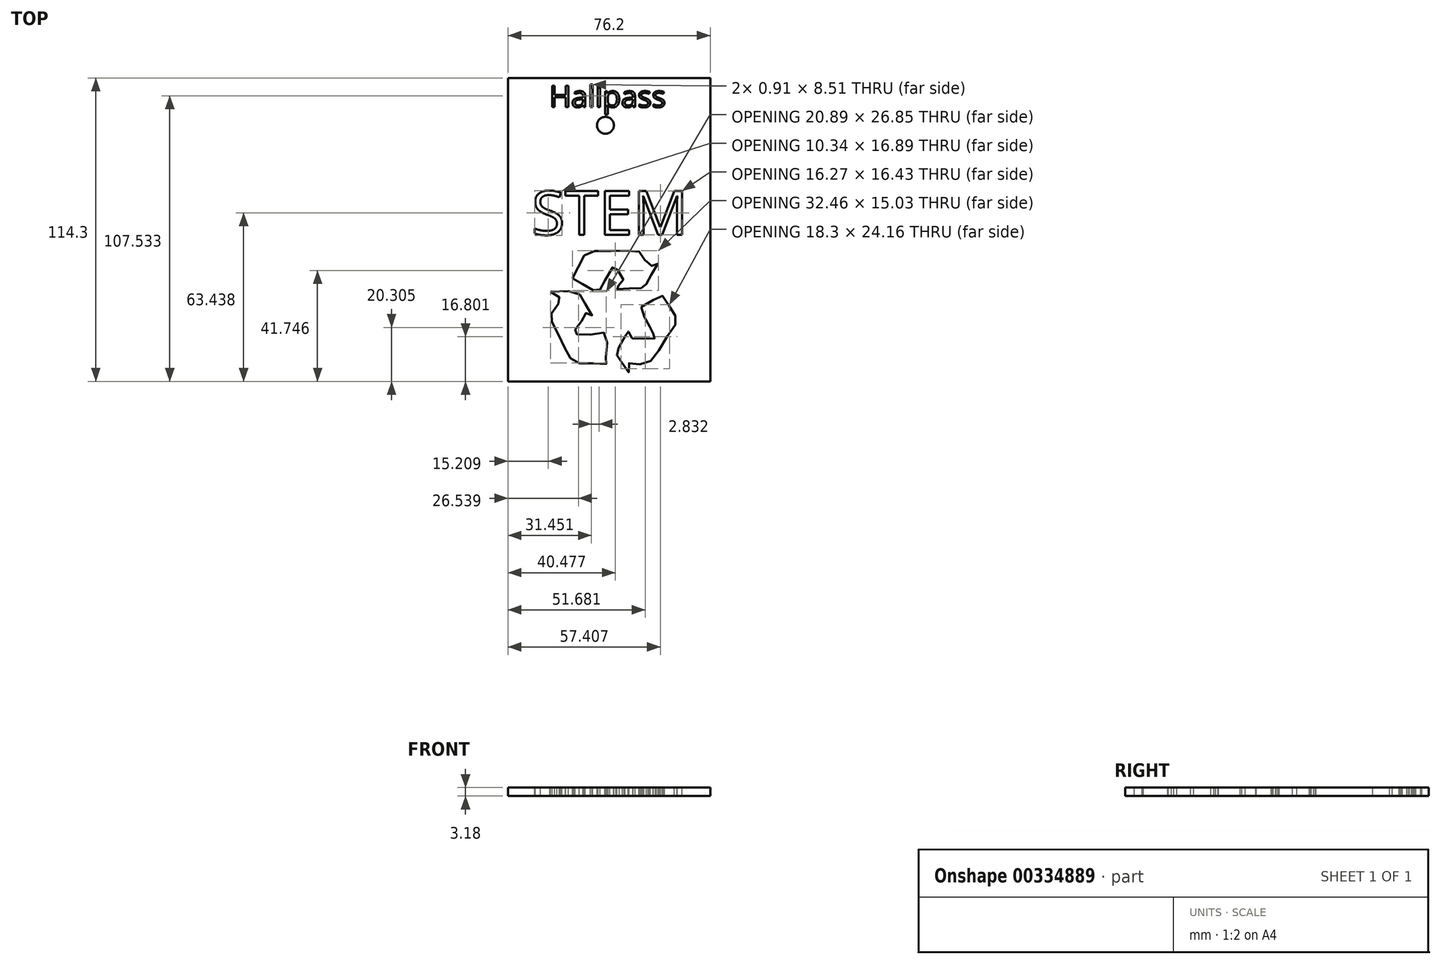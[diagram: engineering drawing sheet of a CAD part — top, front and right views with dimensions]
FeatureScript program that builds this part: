
annotation { "Feature Type Name" : "Feature", "Feature Type Description" : "" }
export const myFeature = defineFeature(function(context is Context, id is Id, definition is map)
    precondition{}
    {
        {
            var Q0;
            Q0=qCreatedBy(makeId("Top.planeOp"),FACE);
            var sketch = newSketch(context, id + "F0", { "sketchPlane" : qUnion([Q0])});
            skLineSegment(sketch, "E0.bottom", {"start": v(-36.95, 59.08) * mm, "end": v(39.25, 59.08) * mm});
            skLineSegment(sketch, "E0.top", {"start": v(-36.95, -55.22) * mm, "end": v(39.25, -55.22) * mm});
            skLineSegment(sketch, "E0.left", {"start": v(-36.95, 59.08) * mm, "end": v(-36.95, -55.22) * mm});
            skLineSegment(sketch, "E0.right", {"start": v(39.25, 59.08) * mm, "end": v(39.25, -55.22) * mm});
            skSolve(sketch);
        }
        {
            var Q0;
            Q0 = qSketchRegion(id + "F0", true);
            extrude(context, id + "F1", {"entities" : qUnion([Q0]), "depth" : 3.17 * mm});
        }
        {
            var Q0;
            Q0=makeQuery(id+"F1.opExtrude","CAP_FACE",FACE,{"disambiguationData":[OSD([sQuery(id+"F0.wireOp",EDGE,"E0.bottom"),sQuery(id+"F0.wireOp",EDGE,"E0.top"),sQuery(id+"F0.wireOp",EDGE,"E0.left"),sQuery(id+"F0.wireOp",EDGE,"E0.right")])],"isStart":false});
            var sketch = newSketch(context, id + "F2", { "sketchPlane" : qUnion([Q0])});
            skCircle(sketch, "E1", {"center": v(-0.25, 41.23) * mm, "radius": 3.18 * mm});
            skSolve(sketch);
        }
        {
            var Q0;
            Q0 = qSketchRegion(id + "F2", true);
            extrude(context, id + "F3", {"entities" : qUnion([Q0]), "operationType" : NewBodyOperationType.REMOVE, "oppositeDirection" : true, "depth" : 3.17 * mm});
        }
        {
            var Q0;
            Q0=makeQuery(id+"F1.opExtrude","CAP_FACE",FACE,{"disambiguationData":[OSD([sQuery(id+"F0.wireOp",EDGE,"E0.bottom"),sQuery(id+"F0.wireOp",EDGE,"E0.top"),sQuery(id+"F0.wireOp",EDGE,"E0.left"),sQuery(id+"F0.wireOp",EDGE,"E0.right")])],"isStart":false});
            var sketch = newSketch(context, id + "F4", { "sketchPlane" : qUnion([Q0])});
            skText(sketch, "E2", { "text": "STEM\n", "fontName": "OpenSans-Regular.ttf"});
            const initialGuessF4  = {"E2": [-0.0281, 0, 1, 0, 0.01657]};
            skSetInitialGuess(sketch, initialGuessF4);
            skSolve(sketch);
        }
        {
            var Q0;
            Q0 = qSketchRegion(id + "F4", true);
            extrude(context, id + "F5", {"entities" : qUnion([Q0]), "operationType" : NewBodyOperationType.REMOVE, "oppositeDirection" : true, "depth" : 3.17 * mm});
        }
        {
            var Q0;
            Q0=qCreatedBy(makeId("Top.planeOp"),FACE);
            var sketch = newSketch(context, id + "F6", { "sketchPlane" : qUnion([Q0])});
            skFitSpline(sketch, "E3", {"points": [v(-12.7, -16.35) * mm, v(-10.74, -17.59) * mm, v(-8.92, -18.6) * mm, v(-7.1, -19.55) * mm, v(-4.78, -20.86) * mm, v(-2.9, -21.88) * mm, v(-2.6, -21.3) * mm, v(-1.8, -19.77) * mm, v(-1.07, -18.46) * mm, v(0, -16.43) * mm, v(1.76, -13.74) * mm, v(3, -11.41) * mm, v(3.58, -11.92) * mm, v(4.38, -13.3) * mm, v(5.25, -14.68) * mm, v(6.27, -16.64) * mm, v(7, -17.73) * mm, v(5.9, -18.53) * mm, v(3.65, -19.84) * mm, v(2.7, -20.35) * mm, v(4.3, -20.42) * mm, v(6.56, -20.35) * mm, v(8.66, -20.2) * mm, v(10.92, -20.13) * mm, v(13.39, -20.13) * mm, v(14.48, -20.06) * mm, v(14.62, -19.62) * mm, v(15.13, -18.68) * mm, v(15.79, -17.3) * mm, v(16.73, -15.55) * mm, v(17.67, -13.67) * mm, v(19.2, -11.41) * mm, v(19.85, -10.1) * mm, v(18.98, -10.54) * mm, v(16.3, -12) * mm, v(15.35, -10.69) * mm, v(14.33, -9.16) * mm, v(13.24, -7.7) * mm, v(12.66, -6.47) * mm, v(11.06, -5.89) * mm, v(8.74, -5.96) * mm, v(4.74, -6.03) * mm, v(0, -6.1) * mm, v(-3.98, -6.03) * mm, v(-6.96, -6.76) * mm, v(-7.98, -7.56) * mm, v(-9, -9.45) * mm, v(-10.45, -12.21) * mm, v(-12.2, -15.2) * mm, v(-12.7, -16.35) * mm]});
            skSolve(sketch);
        }
        {
            var Q0;
            Q0 = qSketchRegion(id + "F6", true);
            extrude(context, id + "F7", {"entities" : qUnion([Q0]), "operationType" : NewBodyOperationType.REMOVE, "depth" : 3.17 * mm});
        }
        {
            var Q0;
            Q0=makeQuery(id+"F1.opExtrude","CAP_FACE",FACE,{"disambiguationData":[OSD([sQuery(id+"F0.wireOp",EDGE,"E0.bottom"),sQuery(id+"F0.wireOp",EDGE,"E0.top"),sQuery(id+"F0.wireOp",EDGE,"E0.left"),sQuery(id+"F0.wireOp",EDGE,"E0.right")])],"isStart":false});
            var sketch = newSketch(context, id + "F8", { "sketchPlane" : qUnion([Q0])});
            skFitSpline(sketch, "E4", {"points": [v(13.23, -27.15) * mm, v(18.2, -24.29) * mm, v(20.94, -22.92) * mm, v(23.32, -25.93) * mm, v(25.33, -29.32) * mm, v(26.7, -32.32) * mm, v(25.33, -34.96) * mm, v(21.32, -40.98) * mm, v(17.8, -46.62) * mm, v(14.8, -48.5) * mm, v(10.53, -48.62) * mm, v(8.4, -48.62) * mm, v(8.53, -51.76) * mm, v(6.65, -49.38) * mm, v(5.14, -46.62) * mm, v(3.76, -44.74) * mm, v(4.52, -42.98) * mm, v(6.65, -39.22) * mm, v(8.4, -35.7) * mm, v(8.4, -38.47) * mm, v(10.4, -38.97) * mm, v(14.17, -39.1) * mm, v(17.93, -39.1) * mm, v(18.93, -38.72) * mm, v(17.93, -37.59) * mm, v(16.93, -35.83) * mm, v(16.05, -33.58) * mm, v(13.8, -30.07) * mm, v(13.23, -27.15) * mm]});
            skSolve(sketch);
        }
        {
            var Q0;
            Q0 = qSketchRegion(id + "F8", true);
            extrude(context, id + "F9", {"entities" : qUnion([Q0]), "operationType" : NewBodyOperationType.REMOVE, "oppositeDirection" : true, "depth" : 3.17 * mm});
        }
        {
            var Q0;
            Q0=makeQuery(id+"F1.opExtrude","CAP_FACE",FACE,{"disambiguationData":[OSD([sQuery(id+"F0.wireOp",EDGE,"E0.bottom"),sQuery(id+"F0.wireOp",EDGE,"E0.top"),sQuery(id+"F0.wireOp",EDGE,"E0.left"),sQuery(id+"F0.wireOp",EDGE,"E0.right")])],"isStart":false});
            var sketch = newSketch(context, id + "F10", { "sketchPlane" : qUnion([Q0])});
            skFitSpline(sketch, "E5", {"points": [v(-20.86, -21.5) * mm, v(-10.36, -21.84) * mm, v(-9.9, -22.53) * mm, v(-7.37, -26.68) * mm, v(-5.3, -30.48) * mm, v(-7.25, -29.45) * mm, v(-8.87, -31.64) * mm, v(-10.02, -33.71) * mm, v(-12.2, -37.06) * mm, v(-11.06, -37.52) * mm, v(-4.6, -37.52) * mm, v(0, -37.29) * mm, v(0, -43.97) * mm, v(0, -47.78) * mm, v(0, -48.7) * mm, v(-5.3, -48.36) * mm, v(-11.4, -48.12) * mm, v(-14.05, -45.47) * mm, v(-16.6, -40.52) * mm, v(-20.05, -33.48) * mm, v(-21.09, -30.71) * mm, v(-18.78, -27.26) * mm, v(-17.4, -24.49) * mm, v(-17.86, -23.34) * mm, v(-20.86, -21.5) * mm]});
            skSolve(sketch);
        }
        {
            var Q0;
            Q0 = qSketchRegion(id + "F10", true);
            extrude(context, id + "F11", {"entities" : qUnion([Q0]), "operationType" : NewBodyOperationType.REMOVE, "oppositeDirection" : true, "depth" : 3.17 * mm});
        }
        {
            var Q0;
            Q0=makeQuery(id+"F1.opExtrude","CAP_FACE",FACE,{"disambiguationData":[OSD([sQuery(id+"F0.wireOp",EDGE,"E0.bottom"),sQuery(id+"F0.wireOp",EDGE,"E0.top"),sQuery(id+"F0.wireOp",EDGE,"E0.left"),sQuery(id+"F0.wireOp",EDGE,"E0.right")])],"isStart":false});
            var sketch = newSketch(context, id + "F12", { "sketchPlane" : qUnion([Q0])});
            skText(sketch, "E6", { "text": "Hallpass\n", "fontName": "OpenSans-Regular.ttf"});
            const initialGuessF12  = {"E6": [-0.0214, 0.04806, 1, 0, 0.00806]};
            skSetInitialGuess(sketch, initialGuessF12);
            skSolve(sketch);
        }
        {
            var Q0;
            Q0 = qSketchRegion(id + "F12", true);
            extrude(context, id + "F13", {"entities" : qUnion([Q0]), "operationType" : NewBodyOperationType.REMOVE, "oppositeDirection" : true, "depth" : 3.17 * mm});
        }
    });
